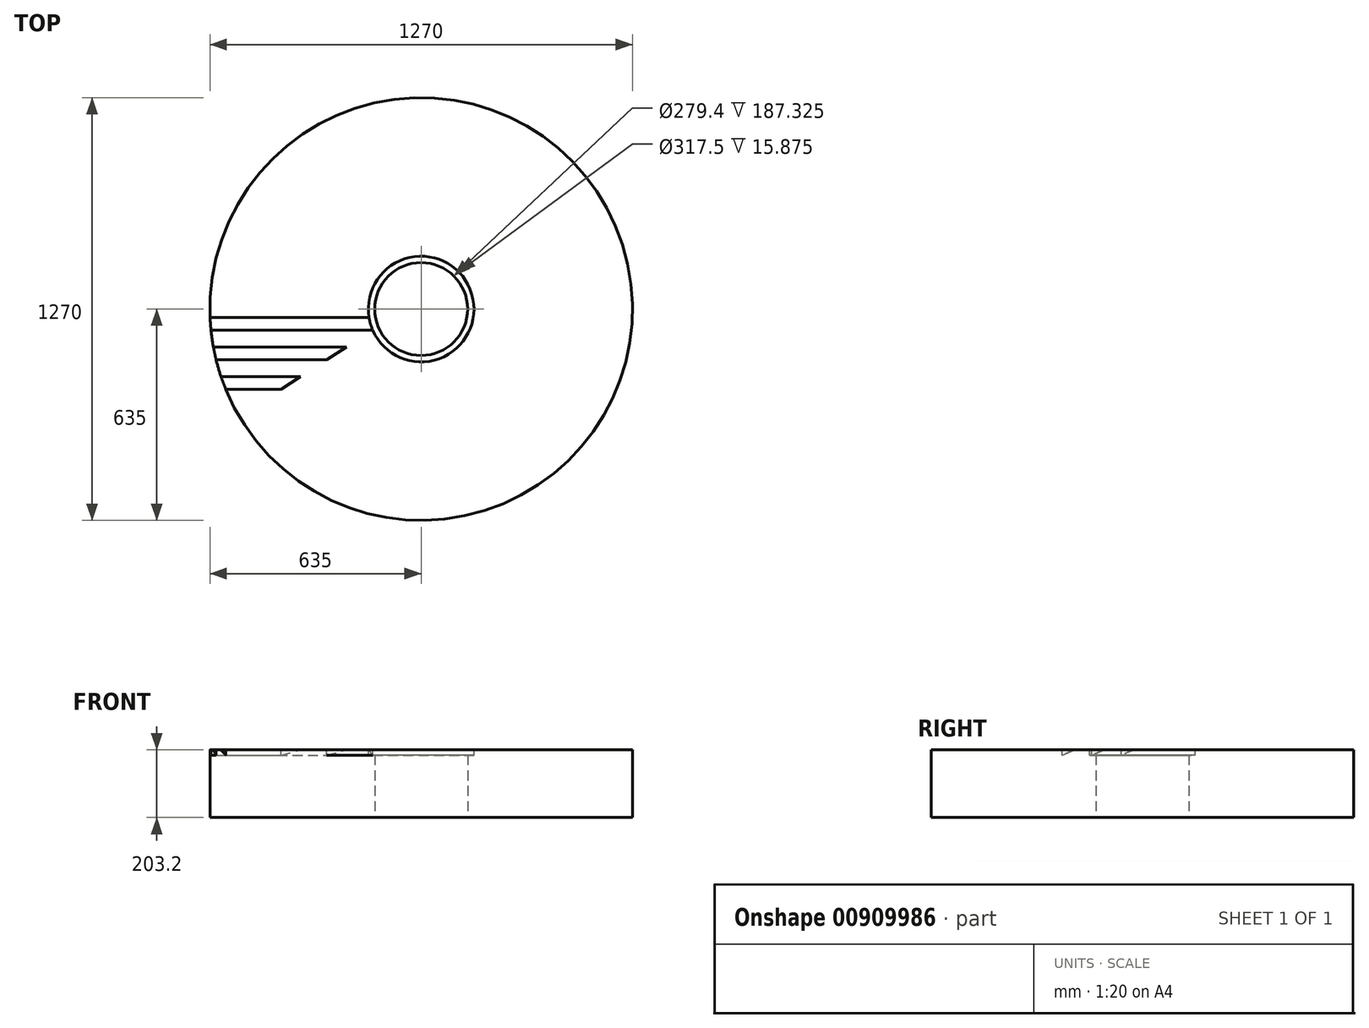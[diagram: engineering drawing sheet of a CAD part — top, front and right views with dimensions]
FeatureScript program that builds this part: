
annotation { "Feature Type Name" : "Feature", "Feature Type Description" : "" }
export const myFeature = defineFeature(function(context is Context, id is Id, definition is map)
    precondition{}
    {
        {
            var Q0;
            Q0=qCreatedBy(makeId("Top.planeOp"),FACE);
            var sketch = newSketch(context, id + "F0", { "sketchPlane" : qUnion([Q0])});
            skCircle(sketch, "E0", {"center": v(0, 0) * mm, "radius": 139.7 * mm});
            skCircle(sketch, "E1", {"center": v(0, 0) * mm, "radius": 635 * mm});
            skSolve(sketch);
        }
        {
            var Q0;
            Q0=makeQuery(id+"F0.imprint","IMPRINT",FACE,{"disambiguationData":[TD([[makeQuery(id+"F0.imprint","IMPRINT",EDGE,{"derivedFrom":sQuery(id+"F0.wireOp",EDGE,"E0")}),-1.0]])]});
            extrude(context, id + "F1", {"entities" : qUnion([Q0]), "depth" : 203.2 * mm, "offsetDistance" : 25 * mm});
        }
        {
            var Q0;
            Q0=makeQuery(id+"F1.opExtrude","CAP_FACE",FACE,{"disambiguationData":[OSD([sQuery(id+"F0.wireOp",EDGE,"E0"),sQuery(id+"F0.wireOp",EDGE,"E1")])],"isStart":false});
            var sketch = newSketch(context, id + "F2", { "sketchPlane" : qUnion([Q0])});
            skLineSegment(sketch, "E2.bottom", {"start": v(-634.5, -25.4) * mm, "end": v(-145.5, -25.4) * mm});
            skLineSegment(sketch, "E2.top", {"start": v(-634.5, -63.5) * mm, "end": v(-145.5, -63.5) * mm});
            skLineSegment(sketch, "E2.left", {"start": v(-634.5, -25.4) * mm, "end": v(-634.5, -63.5) * mm});
            skLineSegment(sketch, "E2.right", {"start": v(-145.5, -25.4) * mm, "end": v(-145.5, -63.5) * mm});
            skLineSegment(sketch, "E3.bottom", {"start": v(-624.63, -114.3) * mm, "end": v(-224.37, -114.3) * mm});
            skLineSegment(sketch, "E3.top", {"start": v(-624.63, -152.4) * mm, "end": v(-283.52, -152.4) * mm});
            skLineSegment(sketch, "E3.left", {"start": v(-624.63, -114.3) * mm, "end": v(-624.63, -152.4) * mm});
            skLineSegment(sketch, "E4.bottom", {"start": v(-601.61, -203.2) * mm, "end": v(-362.4, -203.2) * mm});
            skLineSegment(sketch, "E4.top", {"start": v(-601.61, -241.3) * mm, "end": v(-421.55, -241.3) * mm});
            skLineSegment(sketch, "E4.left", {"start": v(-601.61, -203.2) * mm, "end": v(-601.61, -241.3) * mm});
            skLineSegment(sketch, "E5", {"start": v(-444.25, -25.4) * mm, "end": v(-444.25, -114.3) * mm, "construction": true});
            skLineSegment(sketch, "E6", {"start": v(-444.25, -114.3) * mm, "end": v(-444.25, -203.2) * mm, "construction": true});
            skLineSegment(sketch, "E7", {"start": v(-224.37, -114.3) * mm, "end": v(-283.52, -152.4) * mm});
            skLineSegment(sketch, "E8", {"start": v(-362.4, -203.2) * mm, "end": v(-421.55, -241.3) * mm});
            skCircle(sketch, "E9", {"center": v(0, 0) * mm, "radius": 158.75 * mm});
            skSolve(sketch);
        }
        {
            var Q0;
            {var subQ0=sQuery(id+"F2.wireOp",EDGE,"E9");var subQ1=sQuery(id+"F2.wireOp",EDGE,"E2.bottom");var subQ2=makeQuery(id+"F2.imprint","INTERSECT",VERTEX,{"derivedFrom":[subQ1,subQ0]});Q0=makeQuery(id+"F2.imprint","IMPRINT",FACE,{"disambiguationData":[TD([[makeQuery(id+"F2.imprint","IMPRINT",EDGE,{"disambiguationData":[TD([[subQ2,-1.0]])],"derivedFrom":subQ1}),-1.0]])]});}
            var Q1;
            {var subQ0=sQuery(id+"F2.wireOp",EDGE,"E9");var subQ1=sQuery(id+"F2.wireOp",EDGE,"E2.bottom");var subQ2=makeQuery(id+"F2.imprint","INTERSECT",VERTEX,{"derivedFrom":[subQ1,subQ0]});Q1=makeQuery(id+"F2.imprint","IMPRINT",FACE,{"disambiguationData":[TD([[makeQuery(id+"F2.imprint","IMPRINT",EDGE,{"disambiguationData":[TD([[subQ2,-1.0]])],"derivedFrom":subQ1}),1.0]])]});}
            var Q2;
            Q2=makeQuery(id+"F4.boolean.opBoolean","COPY",FACE,{"derivedFrom":makeQuery(id+"F4.opExtrude","CAP_FACE",FACE,{"disambiguationData":[OSD([sQuery(id+"F0.wireOp",EDGE,"E1"),sQuery(id+"F2.wireOp",EDGE,"E2.bottom"),sQuery(id+"F2.wireOp",EDGE,"E2.top"),sQuery(id+"F2.wireOp",EDGE,"E9")])],"isStart":false})});
            extrude(context, id + "F3", {"entities" : qUnion([Q0, Q1]), "operationType" : NewBodyOperationType.REMOVE, "oppositeDirection" : true, "depth" : 15.88 * mm, "endBoundEntityFace" : qUnion([Q2]), "offsetDistance" : 25 * mm});
        }
        {
            var Q0;
            {var subQ0=sQuery(id+"F2.wireOp",EDGE,"E9");var subQ1=sQuery(id+"F2.wireOp",EDGE,"E2.bottom");var subQ2=makeQuery(id+"F2.imprint","INTERSECT",VERTEX,{"derivedFrom":[subQ1,subQ0]});Q0=makeQuery(id+"F2.imprint","IMPRINT",FACE,{"disambiguationData":[TD([[makeQuery(id+"F2.imprint","IMPRINT",EDGE,{"disambiguationData":[TD([[subQ2,1.0]])],"derivedFrom":subQ1}),-1.0]])]});}
            var Q1;
            {var subQ0=sQuery(id+"F2.wireOp",EDGE,"E3.bottom");Q1=makeQuery(id+"F2.imprint","IMPRINT",FACE,{"disambiguationData":[TD([[makeQuery(id+"F2.imprint","IMPRINT",EDGE,{"derivedFrom":subQ0}),-1.0]])]});}
            var Q2;
            {var subQ0=sQuery(id+"F2.wireOp",EDGE,"E4.bottom");Q2=makeQuery(id+"F2.imprint","IMPRINT",FACE,{"disambiguationData":[TD([[makeQuery(id+"F2.imprint","IMPRINT",EDGE,{"derivedFrom":subQ0}),-1.0]])]});}
            extrude(context, id + "F4", {"entities" : qUnion([Q0, Q1, Q2]), "operationType" : NewBodyOperationType.REMOVE, "oppositeDirection" : true, "depth" : 15.88 * mm, "offsetDistance" : 25 * mm});
        }
        {
            var Q0;
            Q0=makeQuery(id+"F4.boolean.opBoolean","COPY",EDGE,{"derivedFrom":makeQuery(id+"F4.opExtrude","CAP_EDGE",EDGE,{"disambiguationData":[OSD([sQuery(id+"F2.wireOp",EDGE,"E2.bottom")])],"isStart":false})});
            var Q1;
            Q1=makeQuery(id+"F4.boolean.opBoolean","COPY",EDGE,{"derivedFrom":makeQuery(id+"F4.opExtrude","CAP_EDGE",EDGE,{"disambiguationData":[OSD([sQuery(id+"F2.wireOp",EDGE,"E3.bottom")])],"isStart":false})});
            var Q2;
            Q2=makeQuery(id+"F4.boolean.opBoolean","COPY",EDGE,{"derivedFrom":makeQuery(id+"F4.opExtrude","CAP_EDGE",EDGE,{"disambiguationData":[OSD([sQuery(id+"F2.wireOp",EDGE,"E4.bottom")])],"isStart":false})});
            chamfer(context, id + "F5", {"entities" : qUnion([Q0, Q1, Q2]), "chamferType" : ChamferType.TWO_OFFSETS, "width1" : 15.88 * mm, "oppositeDirection" : false, "width2" : 38.1 * mm, "tangentPropagation" : true});
        }
    });
